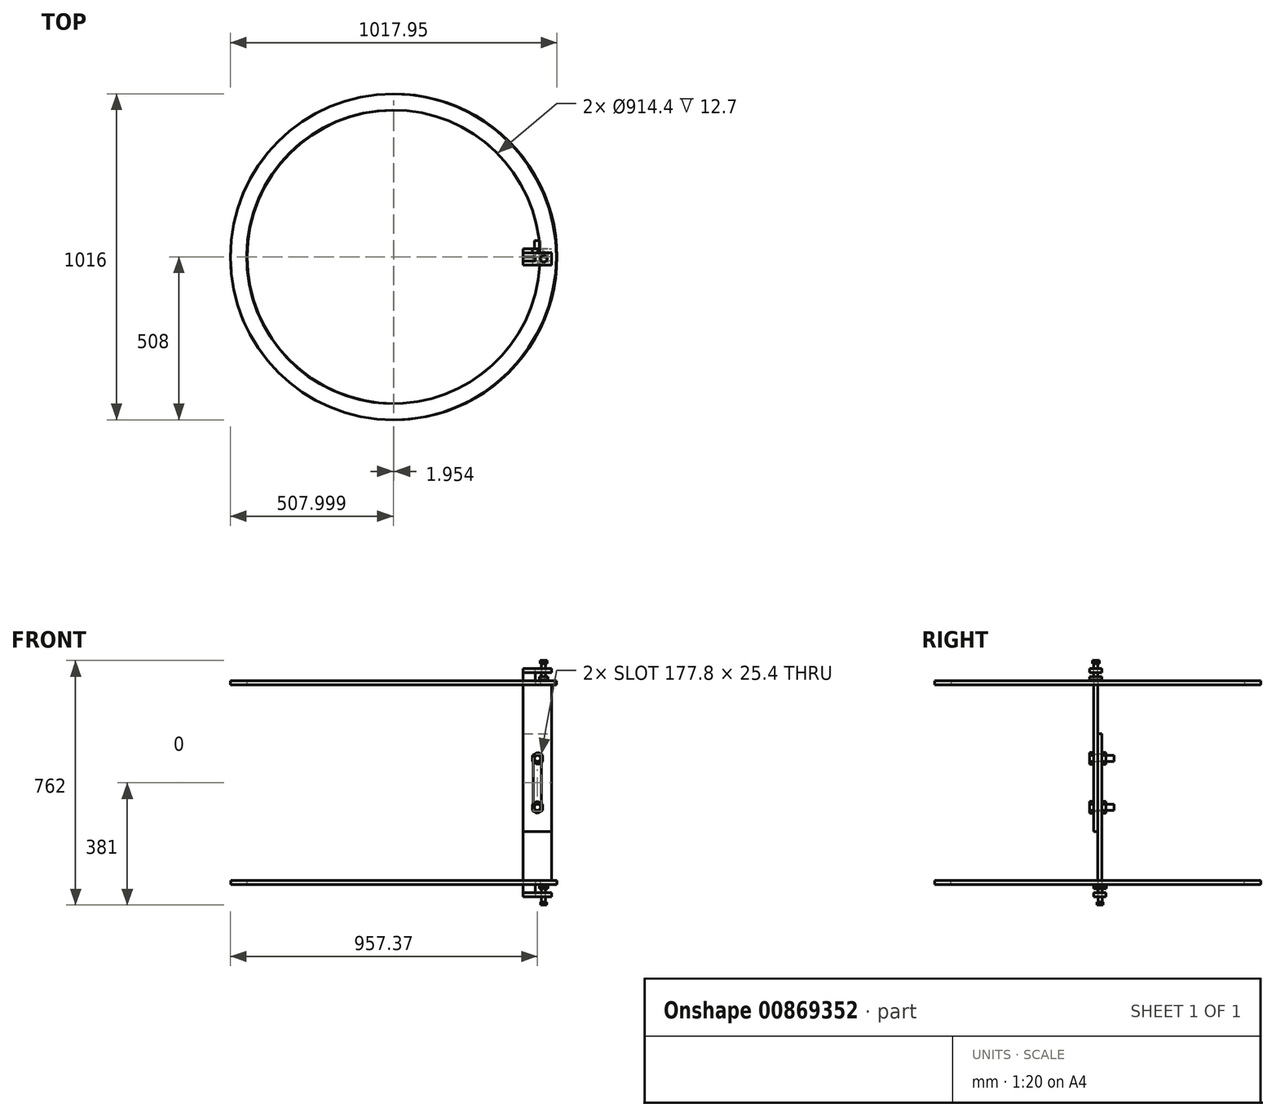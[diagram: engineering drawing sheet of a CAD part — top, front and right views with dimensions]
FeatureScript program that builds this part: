
annotation { "Feature Type Name" : "Feature", "Feature Type Description" : "" }
export const myFeature = defineFeature(function(context is Context, id is Id, definition is map)
    precondition{}
    {
        {
            var Q0;
            Q0=qCreatedBy(makeId("Front.planeOp"),FACE);
            var sketch = newSketch(context, id + "F0", { "sketchPlane" : qUnion([Q0])});
            skLineSegment(sketch, "E0", {"start": v(0, 0) * mm, "end": v(0, 355.6) * mm});
            skLineSegment(sketch, "E1", {"start": v(0, 355.6) * mm, "end": v(38.1, 355.6) * mm});
            skLineSegment(sketch, "E2", {"start": v(38.1, 355.6) * mm, "end": v(38.1, 304.8) * mm});
            skLineSegment(sketch, "E3", {"start": v(38.1, 304.8) * mm, "end": v(88.9, 304.8) * mm});
            skLineSegment(sketch, "E4", {"start": v(88.9, 304.8) * mm, "end": v(88.9, -152.4) * mm});
            skLineSegment(sketch, "E5", {"start": v(88.9, -152.4) * mm, "end": v(0, -152.4) * mm});
            skLineSegment(sketch, "E6", {"start": v(0, -152.4) * mm, "end": v(0, 0) * mm});
            skLineSegment(sketch, "E7.left", {"start": v(31.75, 76.2) * mm, "end": v(31.75, -76.2) * mm});
            skLineSegment(sketch, "E7.right", {"start": v(57.15, 76.2) * mm, "end": v(57.15, -76.2) * mm});
            skPoint(sketch, "E8.firstSnap0", {"position": v(44.45, 0) * mm});
            skPoint(sketch, "E9", {"position": v(44.45, -152.4) * mm});
            skArc(sketch, "E10", {"start": v(57.15, 76.2) * mm, "mid": v(44.45, 88.9) * mm, "end": v(31.75, 76.2) * mm});
            skArc(sketch, "E11", {"start": v(31.75, -76.2) * mm, "mid": v(44.45, -88.9) * mm, "end": v(57.15, -76.2) * mm});
            skSolve(sketch);
        }
        {
            var Q0;
            Q0=makeQuery(id+"F0.imprint","IMPRINT",FACE,{"disambiguationData":[TD([[makeQuery(id+"F0.imprint","IMPRINT",EDGE,{"derivedFrom":sQuery(id+"F0.wireOp",EDGE,"E0")}),-1.0]])]});
            extrude(context, id + "F1", {"entities" : qUnion([Q0]), "depth" : 12.7 * mm, "offsetDistance" : 25.4 * mm});
        }
        {
            var Q0;
            Q0=makeQuery(id+"F1.opExtrude","SWEPT_FACE",FACE,{"disambiguationData":[OSD([sQuery(id+"F0.wireOp",EDGE,"E1")])]});
            var sketch = newSketch(context, id + "F2", { "sketchPlane" : qUnion([Q0])});
            skLineSegment(sketch, "E12.bottom", {"start": v(0, 12.7) * mm, "end": v(88.9, 12.7) * mm});
            skLineSegment(sketch, "E12.top", {"start": v(0, -25.4) * mm, "end": v(88.9, -25.4) * mm});
            skLineSegment(sketch, "E12.left", {"start": v(0, 12.7) * mm, "end": v(0, -25.4) * mm});
            skLineSegment(sketch, "E12.right", {"start": v(88.9, 12.7) * mm, "end": v(88.9, -25.4) * mm});
            skSolve(sketch);
        }
        {
            var Q0;
            {var subQ5=sQuery(id+"F2.wireOp",EDGE,"E12.bottom");Q0=makeQuery(id+"F2.imprint","IMPRINT",FACE,{"disambiguationData":[TD([[makeQuery(id+"F2.imprint","IMPRINT",EDGE,{"derivedFrom":subQ5}),-1.0]])]});}
            extrude(context, id + "F3", {"entities" : qUnion([Q0]), "oppositeDirection" : true, "depth" : 12.7 * mm, "offsetDistance" : 25.4 * mm});
        }
        {
            var Q0;
            Q0=makeQuery(id+"F3.opExtrude","CAP_FACE",FACE,{"disambiguationData":[OSD([sQuery(id+"F0.wireOp",EDGE,"E1"),sQuery(id+"F0.wireOp",EDGE,"E2"),sQuery(id+"F2.wireOp",EDGE,"E12.bottom"),sQuery(id+"F2.wireOp",EDGE,"E12.top"),sQuery(id+"F2.wireOp",EDGE,"E12.left"),sQuery(id+"F2.wireOp",EDGE,"E12.right")])],"isStart":true});
            var sketch = newSketch(context, id + "F4", { "sketchPlane" : qUnion([Q0])});
            skCircle(sketch, "E13", {"center": v(63.5, -6.35) * mm, "radius": 6.35 * mm});
            skSolve(sketch);
        }
        {
            var Q0;
            Q0=makeQuery(id+"F4.imprint","IMPRINT",FACE,{"disambiguationData":[TD([[makeQuery(id+"F4.imprint","IMPRINT",EDGE,{"derivedFrom":sQuery(id+"F4.wireOp",EDGE,"E13")}),1.0]])]});
            var Q1;
            Q1=sQuery(id+"F4.wireOp",EDGE,"E13");
            extrude(context, id + "F5", {"entities" : qUnion([Q0]), "surfaceEntities" : qUnion([Q1]), "depth" : 50.8 * mm, "offsetDistance" : 25.4 * mm, "symmetric" : true});
        }
        {
            var Q0;
            Q0=makeQuery(id+"F5.opExtrude","CAP_FACE",FACE,{"disambiguationData":[OSD([sQuery(id+"F4.wireOp",EDGE,"E13")])],"isStart":true});
            var sketch = newSketch(context, id + "F6", { "sketchPlane" : qUnion([Q0])});
            skLineSegment(sketch, "E14.bottom", {"start": v(49.73, -12.54) * mm, "end": v(77, -12.54) * mm});
            skLineSegment(sketch, "E14.top", {"start": v(49.73, 25.6) * mm, "end": v(77, 25.6) * mm});
            skLineSegment(sketch, "E14.left", {"start": v(49.73, -12.54) * mm, "end": v(49.73, 25.6) * mm});
            skLineSegment(sketch, "E14.right", {"start": v(77, -12.54) * mm, "end": v(77, 25.6) * mm});
            skSolve(sketch);
        }
        {
            var Q0;
            Q0=makeQuery(id+"F6.imprint","IMPRINT",FACE,{"disambiguationData":[TD([[makeQuery(id+"F6.imprint","IMPRINT",EDGE,{"derivedFrom":sQuery(id+"F6.wireOp",EDGE,"E14.bottom")}),1.0]])]});
            extrude(context, id + "F7", {"entities" : qUnion([Q0]), "depth" : 9.52 * mm, "offsetDistance" : 25.4 * mm});
        }
        {
            var Q0;
            Q0=makeQuery(id+"F5.opExtrude","CAP_FACE",FACE,{"disambiguationData":[OSD([sQuery(id+"F4.wireOp",EDGE,"E13")])],"isStart":false});
            var sketch = newSketch(context, id + "F8", { "sketchPlane" : qUnion([Q0])});
            skCircle(sketch, "E15", {"center": v(63.5, -6.35) * mm, "radius": 10.16 * mm});
            skCircle(sketch, "E16.cCircle", {"center": v(63.5, -6.35) * mm, "radius": 10.16 * mm, "construction": true});
            skLineSegment(sketch, "E16.0", {"start": v(69.73, 2.72) * mm, "end": v(74.31, -4.34) * mm});
            skLineSegment(sketch, "E16.1", {"start": v(74.31, -4.34) * mm, "end": v(72.57, -12.58) * mm});
            skLineSegment(sketch, "E16.2", {"start": v(72.57, -12.58) * mm, "end": v(65.5, -17.16) * mm});
            skLineSegment(sketch, "E16.3", {"start": v(65.5, -17.16) * mm, "end": v(57.27, -15.42) * mm});
            skLineSegment(sketch, "E16.4", {"start": v(57.27, -15.42) * mm, "end": v(52.69, -8.36) * mm});
            skLineSegment(sketch, "E16.5", {"start": v(52.69, -8.36) * mm, "end": v(54.43, -0.12) * mm});
            skLineSegment(sketch, "E16.6", {"start": v(54.43, -0.12) * mm, "end": v(61.5, 4.46) * mm});
            skLineSegment(sketch, "E16.7", {"start": v(61.5, 4.46) * mm, "end": v(69.73, 2.72) * mm});
            skPoint(sketch, "E16.0.midPoint", {"position": v(72.02, -0.81) * mm});
            skSolve(sketch);
        }
        {
            var Q0;
            Q0 = qSketchRegion(id + "F8", true);
            extrude(context, id + "F9", {"entities" : qUnion([Q0]), "operationType" : NewBodyOperationType.ADD, "oppositeDirection" : true, "depth" : 9.52 * mm, "offsetDistance" : 25.4 * mm});
        }
        {
            var Q0;
            Q0=qCreatedBy(makeId("Front.planeOp"),FACE);
            var sketch = newSketch(context, id + "F10", { "sketchPlane" : qUnion([Q0])});
            skLineSegment(sketch, "E17", {"start": v(0, 152.4) * mm, "end": v(88.9, 152.4) * mm});
            skLineSegment(sketch, "E18", {"start": v(88.9, 152.4) * mm, "end": v(88.9, -304.8) * mm});
            skLineSegment(sketch, "E19", {"start": v(88.9, -304.8) * mm, "end": v(38.1, -304.8) * mm});
            skLineSegment(sketch, "E20", {"start": v(38.1, -304.8) * mm, "end": v(38.1, -355.6) * mm});
            skLineSegment(sketch, "E21", {"start": v(0, 152.4) * mm, "end": v(0, -355.6) * mm});
            skLineSegment(sketch, "E22", {"start": v(0, -355.6) * mm, "end": v(38.1, -355.6) * mm});
            skArc(sketch, "E23.0", {"start": v(57.15, 76.2) * mm, "mid": v(44.45, 88.9) * mm, "end": v(31.75, 76.2) * mm});
            skLineSegment(sketch, "E23.1", {"start": v(31.75, 76.2) * mm, "end": v(31.75, -76.2) * mm});
            skLineSegment(sketch, "E24.0", {"start": v(57.15, 76.2) * mm, "end": v(57.15, -76.2) * mm});
            skArc(sketch, "E24.1", {"start": v(31.75, -76.2) * mm, "mid": v(44.45, -88.9) * mm, "end": v(57.15, -76.2) * mm});
            skSolve(sketch);
        }
        {
            var Q0;
            Q0=makeQuery(id+"F10.imprint","IMPRINT",FACE,{"disambiguationData":[TD([[makeQuery(id+"F10.imprint","IMPRINT",EDGE,{"derivedFrom":sQuery(id+"F10.wireOp",EDGE,"E17")}),-1.0]])]});
            extrude(context, id + "F11", {"entities" : qUnion([Q0]), "oppositeDirection" : true, "depth" : 12.7 * mm, "offsetDistance" : 25.4 * mm});
        }
        {
            var Q0;
            Q0=makeQuery(id+"F11.opExtrude","SWEPT_FACE",FACE,{"disambiguationData":[OSD([sQuery(id+"F10.wireOp",EDGE,"E22")])]});
            var sketch = newSketch(context, id + "F12", { "sketchPlane" : qUnion([Q0])});
            skLineSegment(sketch, "E25.bottom", {"start": v(0.03, 12.56) * mm, "end": v(88.94, 12.56) * mm});
            skLineSegment(sketch, "E25.top", {"start": v(0.03, -25.54) * mm, "end": v(88.94, -25.54) * mm});
            skLineSegment(sketch, "E25.left", {"start": v(0.03, 12.56) * mm, "end": v(0.03, -25.54) * mm});
            skLineSegment(sketch, "E25.right", {"start": v(88.94, 12.56) * mm, "end": v(88.94, -25.54) * mm});
            skSolve(sketch);
        }
        {
            var Q0;
            Q0 = qSketchRegion(id + "F12", true);
            extrude(context, id + "F13", {"entities" : qUnion([Q0]), "oppositeDirection" : true, "depth" : 12.7 * mm, "offsetDistance" : 25.4 * mm});
        }
        {
            var Q0;
            Q0=makeQuery(id+"F13.opExtrude","CAP_FACE",FACE,{"disambiguationData":[OSD([sQuery(id+"F12.wireOp",EDGE,"E25.bottom"),sQuery(id+"F12.wireOp",EDGE,"E25.top"),sQuery(id+"F12.wireOp",EDGE,"E25.left"),sQuery(id+"F12.wireOp",EDGE,"E25.right")])],"isStart":true});
            var sketch = newSketch(context, id + "F14", { "sketchPlane" : qUnion([Q0])});
            skCircle(sketch, "E26", {"center": v(63.54, -6.5) * mm, "radius": 6.35 * mm});
            skPoint(sketch, "E26.centerSnap0", {"position": v(88.94, -6.5) * mm});
            skSolve(sketch);
        }
        {
            var Q0;
            Q0 = qSketchRegion(id + "F14", true);
            extrude(context, id + "F15", {"entities" : qUnion([Q0]), "depth" : 50.8 * mm, "offsetDistance" : 25.4 * mm, "symmetric" : true});
        }
        {
            var Q0;
            Q0=makeQuery(id+"F15.opExtrude","CAP_FACE",FACE,{"disambiguationData":[OSD([sQuery(id+"F14.wireOp",EDGE,"E26")])],"isStart":true});
            var sketch = newSketch(context, id + "F16", { "sketchPlane" : qUnion([Q0])});
            skLineSegment(sketch, "E27.bottom", {"start": v(49.72, -12.94) * mm, "end": v(77.06, -12.94) * mm});
            skLineSegment(sketch, "E27.top", {"start": v(49.72, 25.98) * mm, "end": v(77.06, 25.98) * mm});
            skLineSegment(sketch, "E27.left", {"start": v(49.72, -12.94) * mm, "end": v(49.72, 25.98) * mm});
            skLineSegment(sketch, "E27.right", {"start": v(77.06, -12.94) * mm, "end": v(77.06, 25.98) * mm});
            skSolve(sketch);
        }
        {
            var Q0;
            Q0 = qSketchRegion(id + "F16", true);
            extrude(context, id + "F17", {"entities" : qUnion([Q0]), "depth" : 9.52 * mm, "offsetDistance" : 25.4 * mm});
        }
        {
            var Q0;
            Q0=makeQuery(id+"F15.opExtrude","CAP_FACE",FACE,{"disambiguationData":[OSD([sQuery(id+"F14.wireOp",EDGE,"E26")])],"isStart":false});
            var sketch = newSketch(context, id + "F18", { "sketchPlane" : qUnion([Q0])});
            skCircle(sketch, "E28", {"center": v(63.54, -6.5) * mm, "radius": 9.53 * mm});
            skCircle(sketch, "E29.cCircle", {"center": v(63.54, -6.5) * mm, "radius": 9.53 * mm, "construction": true});
            skLineSegment(sketch, "E29.0", {"start": v(73.07, -2.55) * mm, "end": v(73.07, -10.44) * mm});
            skLineSegment(sketch, "E29.1", {"start": v(73.07, -10.44) * mm, "end": v(67.49, -16.02) * mm});
            skLineSegment(sketch, "E29.2", {"start": v(67.49, -16.02) * mm, "end": v(59.6, -16.02) * mm});
            skLineSegment(sketch, "E29.3", {"start": v(59.6, -16.02) * mm, "end": v(54.02, -10.44) * mm});
            skLineSegment(sketch, "E29.4", {"start": v(54.02, -10.44) * mm, "end": v(54.02, -2.55) * mm});
            skLineSegment(sketch, "E29.5", {"start": v(54.02, -2.55) * mm, "end": v(59.6, 3.03) * mm});
            skLineSegment(sketch, "E29.6", {"start": v(59.6, 3.03) * mm, "end": v(67.49, 3.03) * mm});
            skLineSegment(sketch, "E29.7", {"start": v(67.49, 3.03) * mm, "end": v(73.07, -2.55) * mm});
            skPoint(sketch, "E29.0.midPoint", {"position": v(73.07, -6.5) * mm});
            skSolve(sketch);
        }
        {
            var Q0;
            Q0 = qSketchRegion(id + "F18", true);
            extrude(context, id + "F19", {"entities" : qUnion([Q0]), "operationType" : NewBodyOperationType.ADD, "oppositeDirection" : true, "depth" : 9.52 * mm, "offsetDistance" : 25.4 * mm});
        }
        {
            var Q0;
            Q0=makeQuery(id+"F1.opExtrude","SWEPT_FACE",FACE,{"disambiguationData":[OSD([sQuery(id+"F0.wireOp",EDGE,"E3")])]});
            var sketch = newSketch(context, id + "F20", { "sketchPlane" : qUnion([Q0])});
            skCircle(sketch, "E30", {"center": v(-404.92, 0) * mm, "radius": 508 * mm});
            skPoint(sketch, "E30.centerSnap0", {"position": v(88.9, -6.35) * mm});
            skCircle(sketch, "E31", {"center": v(-404.92, 0) * mm, "radius": 457.2 * mm});
            skSolve(sketch);
        }
        {
            var Q0;
            {var subQ1=sQuery(id+"F0.wireOp",EDGE,"E3");var subQ6=makeQuery(id+"F1.opExtrude","SWEPT_EDGE",EDGE,{"disambiguationData":[OSD([subQ1,sQuery(id+"F0.wireOp",EDGE,"E4")])]});Q0=makeQuery(id+"F20.imprint","IMPRINT",FACE,{"disambiguationData":[TD([[makeQuery(id+"F20.imprint","IMPRINT",EDGE,{"derivedFrom":subQ6}),1.0]])]});}
            var Q1;
            Q1=makeQuery(id+"F20.imprint","IMPRINT",FACE,{"disambiguationData":[TD([[makeQuery(id+"F20.imprint","IMPRINT",EDGE,{"derivedFrom":sQuery(id+"F20.wireOp",EDGE,"E30")}),1.0]])]});
            extrude(context, id + "F21", {"entities" : qUnion([Q0, Q1]), "depth" : 12.7 * mm, "offsetDistance" : 25.4 * mm});
        }
        {
            var Q0;
            Q0=makeQuery(id+"F11.opExtrude","SWEPT_FACE",FACE,{"disambiguationData":[OSD([sQuery(id+"F10.wireOp",EDGE,"E19")])]});
            var sketch = newSketch(context, id + "F22", { "sketchPlane" : qUnion([Q0])});
            skCircle(sketch, "E32", {"center": v(-402.97, 0) * mm, "radius": 457.2 * mm});
            skCircle(sketch, "E33", {"center": v(-402.97, 0) * mm, "radius": 508 * mm});
            skSolve(sketch);
        }
        {
            var Q0;
            Q0 = qSketchRegion(id + "F22", true);
            extrude(context, id + "F23", {"entities" : qUnion([Q0]), "depth" : 12.7 * mm, "offsetDistance" : 25.4 * mm});
        }
        {
            var Q0;
            Q0=qCreatedBy(makeId("Front.planeOp"),FACE);
            var sketch = newSketch(context, id + "F24", { "sketchPlane" : qUnion([Q0])});
            skCircle(sketch, "E34", {"center": v(44.62, 76.05) * mm, "radius": 9.53 * mm});
            skCircle(sketch, "E35", {"center": v(44.35, -76.25) * mm, "radius": 9.53 * mm});
            skSolve(sketch);
        }
        {
            var Q0;
            Q0 = qSketchRegion(id + "F24", true);
            extrude(context, id + "F25", {"entities" : qUnion([Q0]), "depth" : 25.4 * mm, "offsetDistance" : 25.4 * mm});
        }
        {
            var Q0;
            Q0 = qSketchRegion(id + "F24", true);
            extrude(context, id + "F26", {"entities" : qUnion([Q0]), "oppositeDirection" : true, "depth" : 50.8 * mm, "offsetDistance" : 25.4 * mm});
        }
        {
            var Q0;
            Q0=makeQuery(id+"F25.opExtrude","CAP_FACE",FACE,{"disambiguationData":[OSD([sQuery(id+"F24.wireOp",EDGE,"E34")])],"isStart":false});
            var sketch = newSketch(context, id + "F27", { "sketchPlane" : qUnion([Q0])});
            skCircle(sketch, "E36", {"center": v(44.62, 76.05) * mm, "radius": 15.88 * mm});
            skCircle(sketch, "E37.cCircle", {"center": v(44.62, 76.05) * mm, "radius": 15.88 * mm, "construction": true});
            skLineSegment(sketch, "E37.0", {"start": v(60.5, 85.21) * mm, "end": v(60.5, 66.88) * mm});
            skLineSegment(sketch, "E37.1", {"start": v(60.5, 66.88) * mm, "end": v(44.62, 57.72) * mm});
            skLineSegment(sketch, "E37.2", {"start": v(44.62, 57.72) * mm, "end": v(28.75, 66.88) * mm});
            skLineSegment(sketch, "E37.3", {"start": v(28.75, 66.88) * mm, "end": v(28.75, 85.21) * mm});
            skLineSegment(sketch, "E37.4", {"start": v(28.75, 85.21) * mm, "end": v(44.62, 94.38) * mm});
            skLineSegment(sketch, "E37.5", {"start": v(44.62, 94.38) * mm, "end": v(60.5, 85.21) * mm});
            skPoint(sketch, "E37.0.midPoint", {"position": v(60.5, 76.05) * mm});
            skCircle(sketch, "E38", {"center": v(44.46, -76.13) * mm, "radius": 15.88 * mm});
            skCircle(sketch, "E39.cCircle", {"center": v(44.46, -76.13) * mm, "radius": 15.88 * mm, "construction": true});
            skLineSegment(sketch, "E39.0", {"start": v(60.33, -66.96) * mm, "end": v(60.33, -85.3) * mm});
            skLineSegment(sketch, "E39.1", {"start": v(60.33, -85.3) * mm, "end": v(44.46, -94.46) * mm});
            skLineSegment(sketch, "E39.2", {"start": v(44.46, -94.46) * mm, "end": v(28.58, -85.3) * mm});
            skLineSegment(sketch, "E39.3", {"start": v(28.58, -85.3) * mm, "end": v(28.58, -66.96) * mm});
            skLineSegment(sketch, "E39.4", {"start": v(28.58, -66.96) * mm, "end": v(44.46, -57.8) * mm});
            skLineSegment(sketch, "E39.5", {"start": v(44.46, -57.8) * mm, "end": v(60.33, -66.96) * mm});
            skPoint(sketch, "E39.0.midPoint", {"position": v(60.33, -76.13) * mm});
            skSolve(sketch);
        }
        {
            var Q0;
            Q0 = qSketchRegion(id + "F27", true);
            extrude(context, id + "F28", {"entities" : qUnion([Q0]), "oppositeDirection" : true, "depth" : 12.7 * mm, "offsetDistance" : 25.4 * mm});
        }
        {
            var Q0;
            Q0=makeQuery(id+"F11.opExtrude","CAP_FACE",FACE,{"disambiguationData":[OSD([sQuery(id+"F10.wireOp",EDGE,"E17"),sQuery(id+"F10.wireOp",EDGE,"E18"),sQuery(id+"F10.wireOp",EDGE,"E19"),sQuery(id+"F10.wireOp",EDGE,"E20"),sQuery(id+"F10.wireOp",EDGE,"E21"),sQuery(id+"F10.wireOp",EDGE,"E22"),sQuery(id+"F10.wireOp",EDGE,"E23.0"),sQuery(id+"F10.wireOp",EDGE,"E23.1"),sQuery(id+"F10.wireOp",EDGE,"E24.0"),sQuery(id+"F10.wireOp",EDGE,"E24.1")])],"isStart":false});
            var sketch = newSketch(context, id + "F29", { "sketchPlane" : qUnion([Q0])});
            skCircle(sketch, "E40.0", {"center": v(-44.62, 76.05) * mm, "radius": 15.88 * mm});
            skCircle(sketch, "E40.1", {"center": v(-44.62, 76.05) * mm, "radius": 15.88 * mm});
            skLineSegment(sketch, "E40.2", {"start": v(-60.5, 85.21) * mm, "end": v(-60.5, 66.88) * mm});
            skLineSegment(sketch, "E40.3", {"start": v(-60.5, 66.88) * mm, "end": v(-44.62, 57.72) * mm});
            skLineSegment(sketch, "E40.4", {"start": v(-44.62, 57.72) * mm, "end": v(-28.75, 66.88) * mm});
            skLineSegment(sketch, "E40.5", {"start": v(-28.75, 66.88) * mm, "end": v(-28.75, 85.21) * mm});
            skLineSegment(sketch, "E40.6", {"start": v(-28.75, 85.21) * mm, "end": v(-44.62, 94.38) * mm});
            skLineSegment(sketch, "E40.7", {"start": v(-44.62, 94.38) * mm, "end": v(-60.5, 85.21) * mm});
            skPoint(sketch, "E40.8", {"position": v(-60.5, 76.05) * mm});
            skCircle(sketch, "E40.9", {"center": v(-44.46, -76.13) * mm, "radius": 15.88 * mm});
            skCircle(sketch, "E40.10", {"center": v(-44.46, -76.13) * mm, "radius": 15.88 * mm});
            skLineSegment(sketch, "E40.11", {"start": v(-60.33, -66.96) * mm, "end": v(-60.33, -85.3) * mm});
            skLineSegment(sketch, "E40.12", {"start": v(-60.33, -85.3) * mm, "end": v(-44.46, -94.46) * mm});
            skLineSegment(sketch, "E40.13", {"start": v(-44.46, -94.46) * mm, "end": v(-28.58, -85.3) * mm});
            skLineSegment(sketch, "E40.14", {"start": v(-28.58, -85.3) * mm, "end": v(-28.58, -66.96) * mm});
            skLineSegment(sketch, "E40.15", {"start": v(-28.58, -66.96) * mm, "end": v(-44.46, -57.8) * mm});
            skLineSegment(sketch, "E40.16", {"start": v(-44.46, -57.8) * mm, "end": v(-60.33, -66.96) * mm});
            skPoint(sketch, "E40.17", {"position": v(-60.33, -76.13) * mm});
            skSolve(sketch);
        }
        {
            var Q0;
            Q0 = qSketchRegion(id + "F29", true);
            extrude(context, id + "F30", {"entities" : qUnion([Q0]), "depth" : 12.7 * mm, "offsetDistance" : 25.4 * mm});
        }
    });
